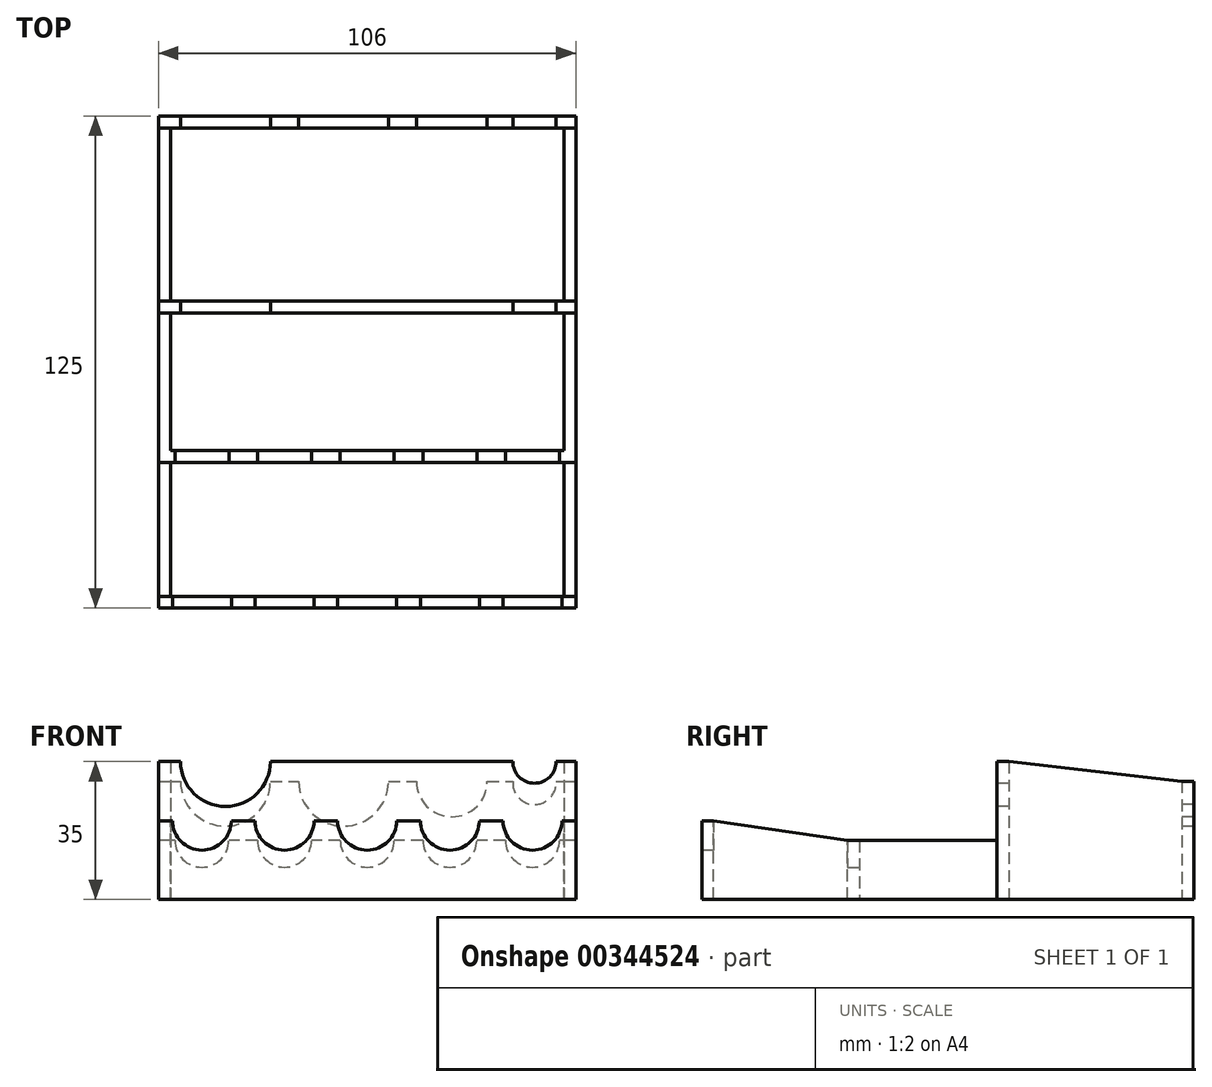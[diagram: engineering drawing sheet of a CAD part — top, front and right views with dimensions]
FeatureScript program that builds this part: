
annotation { "Feature Type Name" : "Feature", "Feature Type Description" : "" }
export const myFeature = defineFeature(function(context is Context, id is Id, definition is map)
    precondition{}
    {
        {
            var Q0;
            Q0=qCreatedBy(makeId("Top.planeOp"),FACE);
            var sketch = newSketch(context, id + "F0", { "sketchPlane" : qUnion([Q0])});
            skLineSegment(sketch, "E0.bottom", {"start": v(53.66, -12.3) * mm, "end": v(-52.34, -12.3) * mm});
            skLineSegment(sketch, "E0.top", {"start": v(53.66, -52.3) * mm, "end": v(-52.34, -52.3) * mm});
            skLineSegment(sketch, "E0.left", {"start": v(53.66, -12.3) * mm, "end": v(53.66, -52.3) * mm});
            skLineSegment(sketch, "E0.right", {"start": v(-52.34, -12.3) * mm, "end": v(-52.34, -52.3) * mm});
            skSolve(sketch);
        }
        {
            var Q0;
            Q0 = qSketchRegion(id + "F0", true);
            extrude(context, id + "F1", {"entities" : qUnion([Q0]), "depth" : 20 * mm});
        }
        {
            var Q0;
            Q0=makeQuery(id+"F1.opExtrude","CAP_FACE",FACE,{"disambiguationData":[OSD([sQuery(id+"F0.wireOp",EDGE,"E0.bottom"),sQuery(id+"F0.wireOp",EDGE,"E0.top"),sQuery(id+"F0.wireOp",EDGE,"E0.left"),sQuery(id+"F0.wireOp",EDGE,"E0.right")])],"isStart":false});
            var sketch = newSketch(context, id + "F2", { "sketchPlane" : qUnion([Q0])});
            skLineSegment(sketch, "E1.0", {"start": v(50.66, -15.3) * mm, "end": v(50.66, -49.3) * mm});
            skLineSegment(sketch, "E1.1", {"start": v(50.66, -15.3) * mm, "end": v(-49.34, -15.3) * mm});
            skLineSegment(sketch, "E1.2", {"start": v(-49.34, -15.3) * mm, "end": v(-49.34, -49.3) * mm});
            skLineSegment(sketch, "E1.3", {"start": v(50.66, -49.3) * mm, "end": v(-49.34, -49.3) * mm});
            skSolve(sketch);
        }
        {
            var Q0;
            Q0=makeQuery(id+"F2.imprint","IMPRINT",FACE,{"disambiguationData":[TD([[makeQuery(id+"F2.imprint","IMPRINT",EDGE,{"derivedFrom":sQuery(id+"F2.wireOp",EDGE,"E1.0")}),-1.0]])]});
            extrude(context, id + "F3", {"entities" : qUnion([Q0]), "operationType" : NewBodyOperationType.REMOVE, "oppositeDirection" : true, "depth" : 20 * mm});
        }
        {
            var Q0;
            Q0=makeQuery(id+"F1.opExtrude","SWEPT_FACE",FACE,{"disambiguationData":[OSD([sQuery(id+"F0.wireOp",EDGE,"E0.top")])]});
            var sketch = newSketch(context, id + "F4", { "sketchPlane" : qUnion([Q0])});
            skCircle(sketch, "E2", {"center": v(-41.34, 20) * mm, "radius": 7.5 * mm});
            skCircle(sketch, "E3.1.0.0", {"center": v(-20.34, 20) * mm, "radius": 7.5 * mm});
            skCircle(sketch, "E3.2.0.0", {"center": v(0.66, 20) * mm, "radius": 7.5 * mm});
            skLineSegment(sketch, "E3.direction1", {"start": v(-41.34, 20) * mm, "end": v(-20.34, 20) * mm, "construction": true});
            skCircle(sketch, "E4.0.3.0", {"center": v(21.66, 20) * mm, "radius": 7.5 * mm});
            skCircle(sketch, "E4.0.4.0", {"center": v(42.66, 20) * mm, "radius": 7.5 * mm});
            skSolve(sketch);
        }
        {
            var Q0;
            {var subQ0=sQuery(id+"F4.wireOp",EDGE,"E2");var subQ1=makeQuery(id+"F1.opExtrude","CAP_EDGE",EDGE,{"disambiguationData":[OSD([sQuery(id+"F0.wireOp",EDGE,"E0.top")])],"isStart":false});var subQ2=makeQuery(id+"F4.imprint","INTERSECT",VERTEX,{"disambiguationData":[OD(0.0)],"derivedFrom":[subQ1,subQ0]});Q0=makeQuery(id+"F4.imprint","IMPRINT",FACE,{"disambiguationData":[TD([[makeQuery(id+"F4.imprint","IMPRINT",EDGE,{"disambiguationData":[TD([[subQ2,-1.0]])],"derivedFrom":subQ0}),1.0]])]});}
            var sketch = newSketch(context, id + "F5", { "sketchPlane" : qUnion([Q0])});
            skSolve(sketch);
        }
        {
            var Q0;
            {var subQ0=sQuery(id+"F4.wireOp",EDGE,"E2");var subQ1=makeQuery(id+"F1.opExtrude","CAP_EDGE",EDGE,{"disambiguationData":[OSD([sQuery(id+"F0.wireOp",EDGE,"E0.top")])],"isStart":false});var subQ2=makeQuery(id+"F4.imprint","INTERSECT",VERTEX,{"disambiguationData":[OD(0.0)],"derivedFrom":[subQ1,subQ0]});Q0=makeQuery(id+"F5.imprint","IMPRINT",FACE,{"disambiguationData":[TD([[makeQuery(id+"F5.imprint","IMPRINT",EDGE,{"derivedFrom":makeQuery(id+"F4.imprint","IMPRINT",EDGE,{"disambiguationData":[TD([[subQ2,-1.0]])],"derivedFrom":subQ0})}),1.0]])]});}
            var Q1;
            {var subQ0=sQuery(id+"F4.wireOp",EDGE,"E4.0.4.0");var subQ1=makeQuery(id+"F1.opExtrude","CAP_EDGE",EDGE,{"disambiguationData":[OSD([sQuery(id+"F0.wireOp",EDGE,"E0.top")])],"isStart":false});var subQ2=makeQuery(id+"F4.imprint","INTERSECT",VERTEX,{"disambiguationData":[OD(0.0)],"derivedFrom":[subQ1,subQ0]});Q1=makeQuery(id+"F4.imprint","IMPRINT",FACE,{"disambiguationData":[TD([[makeQuery(id+"F4.imprint","IMPRINT",EDGE,{"disambiguationData":[TD([[subQ2,1.0]])],"derivedFrom":subQ0}),1.0]])]});}
            var Q2;
            {var subQ0=sQuery(id+"F4.wireOp",EDGE,"E3.1.0.0");var subQ1=makeQuery(id+"F1.opExtrude","CAP_EDGE",EDGE,{"disambiguationData":[OSD([sQuery(id+"F0.wireOp",EDGE,"E0.top")])],"isStart":false});var subQ2=makeQuery(id+"F4.imprint","INTERSECT",VERTEX,{"disambiguationData":[OD(0.0)],"derivedFrom":[subQ1,subQ0]});Q2=makeQuery(id+"F4.imprint","IMPRINT",FACE,{"disambiguationData":[TD([[makeQuery(id+"F4.imprint","IMPRINT",EDGE,{"disambiguationData":[TD([[subQ2,-1.0]])],"derivedFrom":subQ0}),1.0]])]});}
            var Q3;
            {var subQ0=sQuery(id+"F4.wireOp",EDGE,"E3.2.0.0");var subQ1=makeQuery(id+"F1.opExtrude","CAP_EDGE",EDGE,{"disambiguationData":[OSD([sQuery(id+"F0.wireOp",EDGE,"E0.top")])],"isStart":false});var subQ2=makeQuery(id+"F4.imprint","INTERSECT",VERTEX,{"disambiguationData":[OD(0.0)],"derivedFrom":[subQ1,subQ0]});Q3=makeQuery(id+"F4.imprint","IMPRINT",FACE,{"disambiguationData":[TD([[makeQuery(id+"F4.imprint","IMPRINT",EDGE,{"disambiguationData":[TD([[subQ2,-1.0]])],"derivedFrom":subQ0}),1.0]])]});}
            var Q4;
            {var subQ0=sQuery(id+"F4.wireOp",EDGE,"E4.0.3.0");var subQ1=makeQuery(id+"F1.opExtrude","CAP_EDGE",EDGE,{"disambiguationData":[OSD([sQuery(id+"F0.wireOp",EDGE,"E0.top")])],"isStart":false});var subQ2=makeQuery(id+"F4.imprint","INTERSECT",VERTEX,{"disambiguationData":[OD(0.0)],"derivedFrom":[subQ1,subQ0]});Q4=makeQuery(id+"F4.imprint","IMPRINT",FACE,{"disambiguationData":[TD([[makeQuery(id+"F4.imprint","IMPRINT",EDGE,{"disambiguationData":[TD([[subQ2,1.0]])],"derivedFrom":subQ0}),1.0]])]});}
            extrude(context, id + "F6", {"entities" : qUnion([Q0, Q1, Q2, Q3, Q4]), "operationType" : NewBodyOperationType.REMOVE, "oppositeDirection" : true, "depth" : 3 * mm});
        }
        {
            var Q0;
            Q0=makeQuery(id+"F1.opExtrude","SWEPT_FACE",FACE,{"disambiguationData":[OSD([sQuery(id+"F0.wireOp",EDGE,"E0.bottom")])]});
            var sketch = newSketch(context, id + "F7", { "sketchPlane" : qUnion([Q0])});
            skLineSegment(sketch, "E5.bottom", {"start": v(-53.66, 20) * mm, "end": v(52.34, 20) * mm});
            skLineSegment(sketch, "E5.top", {"start": v(-53.66, 15) * mm, "end": v(52.34, 15) * mm});
            skLineSegment(sketch, "E5.left", {"start": v(-53.66, 20) * mm, "end": v(-53.66, 15) * mm});
            skLineSegment(sketch, "E5.right", {"start": v(52.34, 20) * mm, "end": v(52.34, 15) * mm});
            skSolve(sketch);
        }
        {
            var Q0;
            Q0=makeQuery(id+"F7.imprint","IMPRINT",FACE,{"disambiguationData":[TD([[makeQuery(id+"F7.imprint","IMPRINT",EDGE,{"derivedFrom":sQuery(id+"F7.wireOp",EDGE,"E5.bottom")}),-1.0]])]});
            extrude(context, id + "F8", {"entities" : qUnion([Q0]), "operationType" : NewBodyOperationType.REMOVE, "oppositeDirection" : true, "depth" : 3 * mm});
        }
        {
            var Q0;
            {var subQ0=sQuery(id+"F7.wireOp",EDGE,"E5.top");Q0=makeQuery(id+"F7.imprint","IMPRINT",FACE,{"disambiguationData":[TD([[makeQuery(id+"F7.imprint","IMPRINT",EDGE,{"derivedFrom":subQ0}),-1.0]])]});}
            var sketch = newSketch(context, id + "F9", { "sketchPlane" : qUnion([Q0])});
            skCircle(sketch, "E6", {"center": v(41.34, 15) * mm, "radius": 6.85 * mm});
            skCircle(sketch, "E7.1.0.0", {"center": v(20.34, 15) * mm, "radius": 6.85 * mm});
            skCircle(sketch, "E7.2.0.0", {"center": v(-0.66, 15) * mm, "radius": 6.85 * mm});
            skCircle(sketch, "E7.3.0.0", {"center": v(-21.66, 15) * mm, "radius": 6.85 * mm});
            skCircle(sketch, "E7.4.0.0", {"center": v(-42.66, 15) * mm, "radius": 6.85 * mm});
            skLineSegment(sketch, "E7.direction1", {"start": v(41.34, 15) * mm, "end": v(20.34, 15) * mm, "construction": true});
            skSolve(sketch);
        }
        {
            var Q0;
            {var subQ0=sQuery(id+"F9.wireOp",EDGE,"E7.3.0.0");var subQ1=makeQuery(id+"F7.imprint","IMPRINT",EDGE,{"derivedFrom":sQuery(id+"F7.wireOp",EDGE,"E5.top")});var subQ2=makeQuery(id+"F9.imprint","INTERSECT",VERTEX,{"disambiguationData":[OD(0.0)],"derivedFrom":[subQ1,subQ0]});Q0=makeQuery(id+"F9.imprint","IMPRINT",FACE,{"disambiguationData":[TD([[makeQuery(id+"F9.imprint","IMPRINT",EDGE,{"disambiguationData":[TD([[subQ2,-1.0]])],"derivedFrom":subQ0}),1.0]])]});}
            var Q1;
            {var subQ0=sQuery(id+"F9.wireOp",EDGE,"E7.4.0.0");var subQ1=makeQuery(id+"F7.imprint","IMPRINT",EDGE,{"derivedFrom":sQuery(id+"F7.wireOp",EDGE,"E5.top")});var subQ2=makeQuery(id+"F9.imprint","INTERSECT",VERTEX,{"disambiguationData":[OD(0.0)],"derivedFrom":[subQ1,subQ0]});Q1=makeQuery(id+"F9.imprint","IMPRINT",FACE,{"disambiguationData":[TD([[makeQuery(id+"F9.imprint","IMPRINT",EDGE,{"disambiguationData":[TD([[subQ2,-1.0]])],"derivedFrom":subQ0}),1.0]])]});}
            var Q2;
            {var subQ0=sQuery(id+"F9.wireOp",EDGE,"E7.2.0.0");var subQ1=makeQuery(id+"F7.imprint","IMPRINT",EDGE,{"derivedFrom":sQuery(id+"F7.wireOp",EDGE,"E5.top")});var subQ2=makeQuery(id+"F9.imprint","INTERSECT",VERTEX,{"disambiguationData":[OD(0.0)],"derivedFrom":[subQ1,subQ0]});Q2=makeQuery(id+"F9.imprint","IMPRINT",FACE,{"disambiguationData":[TD([[makeQuery(id+"F9.imprint","IMPRINT",EDGE,{"disambiguationData":[TD([[subQ2,1.0]])],"derivedFrom":subQ0}),1.0]])]});}
            var Q3;
            {var subQ0=sQuery(id+"F9.wireOp",EDGE,"E7.1.0.0");var subQ1=makeQuery(id+"F7.imprint","IMPRINT",EDGE,{"derivedFrom":sQuery(id+"F7.wireOp",EDGE,"E5.top")});var subQ2=makeQuery(id+"F9.imprint","INTERSECT",VERTEX,{"disambiguationData":[OD(0.0)],"derivedFrom":[subQ1,subQ0]});Q3=makeQuery(id+"F9.imprint","IMPRINT",FACE,{"disambiguationData":[TD([[makeQuery(id+"F9.imprint","IMPRINT",EDGE,{"disambiguationData":[TD([[subQ2,1.0]])],"derivedFrom":subQ0}),1.0]])]});}
            var Q4;
            {var subQ0=sQuery(id+"F9.wireOp",EDGE,"E6");var subQ1=makeQuery(id+"F7.imprint","IMPRINT",EDGE,{"derivedFrom":sQuery(id+"F7.wireOp",EDGE,"E5.top")});var subQ2=makeQuery(id+"F9.imprint","INTERSECT",VERTEX,{"disambiguationData":[OD(0.0)],"derivedFrom":[subQ1,subQ0]});Q4=makeQuery(id+"F9.imprint","IMPRINT",FACE,{"disambiguationData":[TD([[makeQuery(id+"F9.imprint","IMPRINT",EDGE,{"disambiguationData":[TD([[subQ2,1.0]])],"derivedFrom":subQ0}),1.0]])]});}
            extrude(context, id + "F10", {"entities" : qUnion([Q0, Q1, Q2, Q3, Q4]), "operationType" : NewBodyOperationType.REMOVE, "oppositeDirection" : true, "depth" : 3 * mm});
        }
        {
            var Q0;
            Q0=makeQuery(id+"F1.opExtrude","SWEPT_FACE",FACE,{"disambiguationData":[OSD([sQuery(id+"F0.wireOp",EDGE,"E0.left")])]});
            var sketch = newSketch(context, id + "F11", { "sketchPlane" : qUnion([Q0])});
            skLineSegment(sketch, "E8.bottom", {"start": v(-12.3, 15) * mm, "end": v(22.7, 15) * mm});
            skLineSegment(sketch, "E8.top", {"start": v(-12.3, 0) * mm, "end": v(22.7, 0) * mm});
            skLineSegment(sketch, "E8.left", {"start": v(-12.3, 15) * mm, "end": v(-12.3, 0) * mm});
            skLineSegment(sketch, "E8.right", {"start": v(22.7, 15) * mm, "end": v(22.7, 0) * mm});
            skSolve(sketch);
        }
        {
            var Q0;
            Q0=makeQuery(id+"F1.opExtrude","SWEPT_FACE",FACE,{"disambiguationData":[OSD([sQuery(id+"F0.wireOp",EDGE,"E0.right")])]});
            var sketch = newSketch(context, id + "F12", { "sketchPlane" : qUnion([Q0])});
            skLineSegment(sketch, "E9.bottom", {"start": v(12.3, 15) * mm, "end": v(-22.7, 15) * mm});
            skLineSegment(sketch, "E9.top", {"start": v(12.3, 0) * mm, "end": v(-22.7, 0) * mm});
            skLineSegment(sketch, "E9.left", {"start": v(12.3, 15) * mm, "end": v(12.3, 0) * mm});
            skLineSegment(sketch, "E9.right", {"start": v(-22.7, 15) * mm, "end": v(-22.7, 0) * mm});
            skSolve(sketch);
        }
        {
            var Q0;
            Q0=makeQuery(id+"F12.imprint","IMPRINT",FACE,{"disambiguationData":[TD([[makeQuery(id+"F12.imprint","IMPRINT",EDGE,{"derivedFrom":sQuery(id+"F12.wireOp",EDGE,"E9.bottom")}),1.0]])]});
            extrude(context, id + "F13", {"entities" : qUnion([Q0]), "operationType" : NewBodyOperationType.ADD, "oppositeDirection" : true, "depth" : 3 * mm});
        }
        {
            var Q0;
            Q0=makeQuery(id+"F11.imprint","IMPRINT",FACE,{"disambiguationData":[TD([[makeQuery(id+"F11.imprint","IMPRINT",EDGE,{"derivedFrom":sQuery(id+"F11.wireOp",EDGE,"E8.bottom")}),-1.0]])]});
            extrude(context, id + "F14", {"entities" : qUnion([Q0]), "operationType" : NewBodyOperationType.ADD, "oppositeDirection" : true, "depth" : 3 * mm});
        }
        {
            var Q0;
            Q0=makeQuery(id+"F14.boolean.opBoolean","MERGE",FACE,{"derivedFrom":[makeQuery(id+"F13.boolean.opBoolean","MERGE",FACE,{"derivedFrom":[makeQuery(id+"F1.opExtrude","CAP_FACE",FACE,{"disambiguationData":[OSD([sQuery(id+"F0.wireOp",EDGE,"E0.bottom"),sQuery(id+"F0.wireOp",EDGE,"E0.top"),sQuery(id+"F0.wireOp",EDGE,"E0.left"),sQuery(id+"F0.wireOp",EDGE,"E0.right")])],"isStart":true}),makeQuery(id+"F13.opExtrude","SWEPT_FACE",FACE,{"disambiguationData":[OSD([sQuery(id+"F12.wireOp",EDGE,"E9.top")])]})]}),makeQuery(id+"F14.opExtrude","SWEPT_FACE",FACE,{"disambiguationData":[OSD([sQuery(id+"F11.wireOp",EDGE,"E8.top")])]})]});
            var sketch = newSketch(context, id + "F15", { "sketchPlane" : qUnion([Q0])});
            skLineSegment(sketch, "E10.bottom", {"start": v(-52.34, -22.7) * mm, "end": v(53.66, -22.7) * mm});
            skLineSegment(sketch, "E10.top", {"start": v(-52.34, -72.7) * mm, "end": v(53.66, -72.7) * mm});
            skLineSegment(sketch, "E10.left", {"start": v(-52.34, -22.7) * mm, "end": v(-52.34, -72.7) * mm});
            skLineSegment(sketch, "E10.right", {"start": v(53.66, -22.7) * mm, "end": v(53.66, -72.7) * mm});
            skLineSegment(sketch, "E11.0", {"start": v(-49.34, -25.7) * mm, "end": v(-49.34, -69.7) * mm});
            skLineSegment(sketch, "E11.1", {"start": v(-49.34, -25.7) * mm, "end": v(50.66, -25.7) * mm});
            skLineSegment(sketch, "E11.2", {"start": v(50.66, -25.7) * mm, "end": v(50.66, -69.7) * mm});
            skLineSegment(sketch, "E11.3", {"start": v(-49.34, -69.7) * mm, "end": v(50.66, -69.7) * mm});
            skSolve(sketch);
        }
        {
            var Q0;
            Q0=makeQuery(id+"F15.imprint","IMPRINT",FACE,{"disambiguationData":[TD([[makeQuery(id+"F15.imprint","IMPRINT",EDGE,{"derivedFrom":sQuery(id+"F15.wireOp",EDGE,"E10.top")}),1.0]])]});
            extrude(context, id + "F16", {"entities" : qUnion([Q0]), "oppositeDirection" : true, "depth" : 35 * mm});
        }
        {
            var Q0;
            Q0=makeQuery(id+"F16.opExtrude","SWEPT_FACE",FACE,{"disambiguationData":[OSD([sQuery(id+"F15.wireOp",EDGE,"E10.bottom")])]});
            var sketch = newSketch(context, id + "F17", { "sketchPlane" : qUnion([Q0])});
            skCircle(sketch, "E12", {"center": v(-35.34, 35) * mm, "radius": 11.4 * mm});
            skCircle(sketch, "E13", {"center": v(43.16, 35) * mm, "radius": 5.5 * mm});
            skCircle(sketch, "E14", {"center": v(-7.84, 35) * mm, "radius": 9 * mm});
            skCircle(sketch, "E15.1.0.0", {"center": v(20.69, 35) * mm, "radius": 9 * mm});
            skLineSegment(sketch, "E15.direction1", {"start": v(-7.84, 35) * mm, "end": v(20.69, 35) * mm, "construction": true});
            skSolve(sketch);
        }
        {
            var Q0;
            {var subQ0=sQuery(id+"F17.wireOp",EDGE,"E12");var subQ1=makeQuery(id+"F16.opExtrude","CAP_EDGE",EDGE,{"disambiguationData":[OSD([sQuery(id+"F15.wireOp",EDGE,"E10.bottom")])],"isStart":false});var subQ2=makeQuery(id+"F17.imprint","INTERSECT",VERTEX,{"disambiguationData":[OD(0.0)],"derivedFrom":[subQ1,subQ0]});Q0=makeQuery(id+"F17.imprint","IMPRINT",FACE,{"disambiguationData":[TD([[makeQuery(id+"F17.imprint","IMPRINT",EDGE,{"disambiguationData":[TD([[subQ2,-1.0]])],"derivedFrom":subQ0}),1.0]])]});}
            var Q1;
            {var subQ0=sQuery(id+"F17.wireOp",EDGE,"8cf82a59-2f2f-4f61-8bf0-19492cf728df.1.0.0");var subQ1=makeQuery(id+"F16.opExtrude","CAP_EDGE",EDGE,{"disambiguationData":[OSD([sQuery(id+"F15.wireOp",EDGE,"E10.bottom")])],"isStart":false});var subQ2=makeQuery(id+"F17.imprint","INTERSECT",VERTEX,{"disambiguationData":[OD(0.0)],"derivedFrom":[subQ1,subQ0]});Q1=makeQuery(id+"F17.imprint","IMPRINT",FACE,{"disambiguationData":[TD([[makeQuery(id+"F17.imprint","IMPRINT",EDGE,{"disambiguationData":[TD([[subQ2,-1.0]])],"derivedFrom":subQ0}),1.0]])]});}
            var Q2;
            {var subQ0=sQuery(id+"F17.wireOp",EDGE,"E14");var subQ1=makeQuery(id+"F16.opExtrude","CAP_EDGE",EDGE,{"disambiguationData":[OSD([sQuery(id+"F15.wireOp",EDGE,"E10.bottom")])],"isStart":false});var subQ2=makeQuery(id+"F17.imprint","INTERSECT",VERTEX,{"disambiguationData":[OD(0.0)],"derivedFrom":[subQ1,subQ0]});Q2=makeQuery(id+"F17.imprint","IMPRINT",FACE,{"disambiguationData":[TD([[makeQuery(id+"F17.imprint","IMPRINT",EDGE,{"disambiguationData":[TD([[subQ2,1.0]])],"derivedFrom":subQ0}),1.0]])]});}
            var Q3;
            {var subQ0=sQuery(id+"F17.wireOp",EDGE,"E13");var subQ1=makeQuery(id+"F16.opExtrude","CAP_EDGE",EDGE,{"disambiguationData":[OSD([sQuery(id+"F15.wireOp",EDGE,"E10.bottom")])],"isStart":false});var subQ2=makeQuery(id+"F17.imprint","INTERSECT",VERTEX,{"disambiguationData":[OD(0.0)],"derivedFrom":[subQ1,subQ0]});Q3=makeQuery(id+"F17.imprint","IMPRINT",FACE,{"disambiguationData":[TD([[makeQuery(id+"F17.imprint","IMPRINT",EDGE,{"disambiguationData":[TD([[subQ2,1.0]])],"derivedFrom":subQ0}),1.0]])]});}
            extrude(context, id + "F18", {"entities" : qUnion([Q0, Q1, Q2, Q3]), "operationType" : NewBodyOperationType.REMOVE, "oppositeDirection" : true, "depth" : 3 * mm});
        }
        {
            var Q0;
            Q0=makeQuery(id+"F3.boolean.opBoolean","COPY",FACE,{"derivedFrom":makeQuery(id+"F3.opExtrude","SWEPT_FACE",FACE,{"disambiguationData":[OSD([sQuery(id+"F2.wireOp",EDGE,"E1.0")])]})});
            var sketch = newSketch(context, id + "F19", { "sketchPlane" : qUnion([Q0])});
            skLineSegment(sketch, "E16", {"start": v(49.3, 20) * mm, "end": v(15.3, 15) * mm});
            skSolve(sketch);
        }
        {
            var Q0;
            Q0=makeQuery(id+"F19.imprint","IMPRINT",FACE,{"disambiguationData":[TD([[makeQuery(id+"F19.imprint","IMPRINT",EDGE,{"derivedFrom":sQuery(id+"F19.wireOp",EDGE,"E16")}),-1.0]])]});
            extrude(context, id + "F20", {"entities" : qUnion([Q0]), "operationType" : NewBodyOperationType.REMOVE, "oppositeDirection" : true, "depth" : 3 * mm});
        }
        {
            var Q0;
            Q0=makeQuery(id+"F3.boolean.opBoolean","COPY",FACE,{"derivedFrom":makeQuery(id+"F3.opExtrude","SWEPT_FACE",FACE,{"disambiguationData":[OSD([sQuery(id+"F2.wireOp",EDGE,"E1.2")])]})});
            var sketch = newSketch(context, id + "F21", { "sketchPlane" : qUnion([Q0])});
            skLineSegment(sketch, "E17", {"start": v(-49.3, 20) * mm, "end": v(-15.3, 15) * mm});
            skSolve(sketch);
        }
        {
            var Q0;
            Q0=makeQuery(id+"F21.imprint","IMPRINT",FACE,{"disambiguationData":[TD([[makeQuery(id+"F21.imprint","IMPRINT",EDGE,{"derivedFrom":sQuery(id+"F21.wireOp",EDGE,"E17")}),1.0]])]});
            extrude(context, id + "F22", {"entities" : qUnion([Q0]), "operationType" : NewBodyOperationType.REMOVE, "oppositeDirection" : true, "depth" : 3 * mm});
        }
        {
            var Q0;
            Q0=makeQuery(id+"F16.opExtrude","SWEPT_FACE",FACE,{"disambiguationData":[OSD([sQuery(id+"F15.wireOp",EDGE,"E10.top")])]});
            var sketch = newSketch(context, id + "F23", { "sketchPlane" : qUnion([Q0])});
            skLineSegment(sketch, "E18.bottom", {"start": v(52.34, 35) * mm, "end": v(-53.66, 35) * mm});
            skLineSegment(sketch, "E18.top", {"start": v(52.34, 30) * mm, "end": v(-53.66, 30) * mm});
            skLineSegment(sketch, "E18.left", {"start": v(52.34, 35) * mm, "end": v(52.34, 30) * mm});
            skLineSegment(sketch, "E18.right", {"start": v(-53.66, 35) * mm, "end": v(-53.66, 30) * mm});
            skSolve(sketch);
        }
        {
            var Q0;
            Q0=makeQuery(id+"F23.imprint","IMPRINT",FACE,{"disambiguationData":[TD([[makeQuery(id+"F23.imprint","IMPRINT",EDGE,{"derivedFrom":sQuery(id+"F23.wireOp",EDGE,"E18.bottom")}),1.0]])]});
            extrude(context, id + "F24", {"entities" : qUnion([Q0]), "operationType" : NewBodyOperationType.REMOVE, "oppositeDirection" : true, "depth" : 3 * mm});
        }
        {
            var Q0;
            Q0=makeQuery(id+"F16.opExtrude","SWEPT_FACE",FACE,{"disambiguationData":[OSD([sQuery(id+"F15.wireOp",EDGE,"E11.0")])]});
            var sketch = newSketch(context, id + "F25", { "sketchPlane" : qUnion([Q0])});
            skLineSegment(sketch, "E19", {"start": v(25.7, 35) * mm, "end": v(69.7, 30) * mm});
            skSolve(sketch);
        }
        {
            var Q0;
            Q0=makeQuery(id+"F25.imprint","IMPRINT",FACE,{"disambiguationData":[TD([[makeQuery(id+"F25.imprint","IMPRINT",EDGE,{"derivedFrom":sQuery(id+"F25.wireOp",EDGE,"E19")}),1.0]])]});
            extrude(context, id + "F26", {"entities" : qUnion([Q0]), "operationType" : NewBodyOperationType.REMOVE, "oppositeDirection" : true, "depth" : 3 * mm});
        }
        {
            var Q0;
            Q0=makeQuery(id+"F16.opExtrude","SWEPT_FACE",FACE,{"disambiguationData":[OSD([sQuery(id+"F15.wireOp",EDGE,"E11.2")])]});
            var sketch = newSketch(context, id + "F27", { "sketchPlane" : qUnion([Q0])});
            skLineSegment(sketch, "E20", {"start": v(-25.7, 35) * mm, "end": v(-69.7, 30) * mm});
            skSolve(sketch);
        }
        {
            var Q0;
            Q0=makeQuery(id+"F27.imprint","IMPRINT",FACE,{"disambiguationData":[TD([[makeQuery(id+"F27.imprint","IMPRINT",EDGE,{"derivedFrom":sQuery(id+"F27.wireOp",EDGE,"E20")}),-1.0]])]});
            extrude(context, id + "F28", {"entities" : qUnion([Q0]), "operationType" : NewBodyOperationType.REMOVE, "oppositeDirection" : true, "depth" : 3 * mm});
        }
        {
            var Q0;
            Q0=makeQuery(id+"F16.opExtrude","SWEPT_FACE",FACE,{"disambiguationData":[OSD([sQuery(id+"F15.wireOp",EDGE,"E11.3")])]});
            var sketch = newSketch(context, id + "F29", { "sketchPlane" : qUnion([Q0])});
            skCircle(sketch, "E21", {"center": v(-35.34, 30) * mm, "radius": 11.4 * mm});
            skCircle(sketch, "E22", {"center": v(43.16, 29.6) * mm, "radius": 5.5 * mm});
            skCircle(sketch, "E23.1.0.0", {"center": v(-5.34, 30) * mm, "radius": 11.4 * mm});
            skLineSegment(sketch, "E23.direction1", {"start": v(-35.34, 30) * mm, "end": v(-5.34, 30) * mm, "construction": true});
            skCircle(sketch, "E24", {"center": v(22.16, 30) * mm, "radius": 9 * mm});
            skSolve(sketch);
        }
        {
            var Q0;
            {var subQ0=sQuery(id+"F29.wireOp",EDGE,"E22");var subQ1=sQuery(id+"F23.wireOp",EDGE,"E18.top");var subQ2=makeQuery(id+"F24.boolean.opBoolean","COPY",EDGE,{"disambiguationData":[topologyDisambiguationEdgeConnected([makeQuery(id+"F16.opExtrude","SWEPT_FACE",FACE,{"disambiguationData":[OSD([sQuery(id+"F15.wireOp",EDGE,"E11.3")])]}),makeQuery(id+"F24.opExtrude","SWEPT_FACE",FACE,{"disambiguationData":[OSD([subQ1])]})])],"derivedFrom":makeQuery(id+"F24.opExtrude","CAP_EDGE",EDGE,{"disambiguationData":[OSD([subQ1])],"isStart":false})});var subQ3=makeQuery(id+"F29.imprint","INTERSECT",VERTEX,{"disambiguationData":[OD(0.0)],"derivedFrom":[subQ2,subQ0]});Q0=makeQuery(id+"F29.imprint","IMPRINT",FACE,{"disambiguationData":[TD([[makeQuery(id+"F29.imprint","IMPRINT",EDGE,{"disambiguationData":[TD([[subQ3,1.0]])],"derivedFrom":subQ0}),1.0]])]});}
            var Q1;
            {var subQ0=sQuery(id+"F29.wireOp",EDGE,"E24");var subQ1=sQuery(id+"F23.wireOp",EDGE,"E18.top");var subQ2=makeQuery(id+"F24.boolean.opBoolean","COPY",EDGE,{"disambiguationData":[topologyDisambiguationEdgeConnected([makeQuery(id+"F16.opExtrude","SWEPT_FACE",FACE,{"disambiguationData":[OSD([sQuery(id+"F15.wireOp",EDGE,"E11.3")])]}),makeQuery(id+"F24.opExtrude","SWEPT_FACE",FACE,{"disambiguationData":[OSD([subQ1])]})])],"derivedFrom":makeQuery(id+"F24.opExtrude","CAP_EDGE",EDGE,{"disambiguationData":[OSD([subQ1])],"isStart":false})});var subQ3=makeQuery(id+"F29.imprint","INTERSECT",VERTEX,{"disambiguationData":[OD(0.0)],"derivedFrom":[subQ2,subQ0]});Q1=makeQuery(id+"F29.imprint","IMPRINT",FACE,{"disambiguationData":[TD([[makeQuery(id+"F29.imprint","IMPRINT",EDGE,{"disambiguationData":[TD([[subQ3,1.0]])],"derivedFrom":subQ0}),1.0]])]});}
            var Q2;
            {var subQ0=sQuery(id+"F29.wireOp",EDGE,"E23.1.0.0");var subQ1=sQuery(id+"F23.wireOp",EDGE,"E18.top");var subQ2=makeQuery(id+"F24.boolean.opBoolean","COPY",EDGE,{"disambiguationData":[topologyDisambiguationEdgeConnected([makeQuery(id+"F16.opExtrude","SWEPT_FACE",FACE,{"disambiguationData":[OSD([sQuery(id+"F15.wireOp",EDGE,"E11.3")])]}),makeQuery(id+"F24.opExtrude","SWEPT_FACE",FACE,{"disambiguationData":[OSD([subQ1])]})])],"derivedFrom":makeQuery(id+"F24.opExtrude","CAP_EDGE",EDGE,{"disambiguationData":[OSD([subQ1])],"isStart":false})});var subQ3=makeQuery(id+"F29.imprint","INTERSECT",VERTEX,{"disambiguationData":[OD(0.0)],"derivedFrom":[subQ2,subQ0]});Q2=makeQuery(id+"F29.imprint","IMPRINT",FACE,{"disambiguationData":[TD([[makeQuery(id+"F29.imprint","IMPRINT",EDGE,{"disambiguationData":[TD([[subQ3,-1.0]])],"derivedFrom":subQ0}),1.0]])]});}
            var Q3;
            {var subQ0=sQuery(id+"F29.wireOp",EDGE,"E21");var subQ1=sQuery(id+"F23.wireOp",EDGE,"E18.top");var subQ2=makeQuery(id+"F24.boolean.opBoolean","COPY",EDGE,{"disambiguationData":[topologyDisambiguationEdgeConnected([makeQuery(id+"F16.opExtrude","SWEPT_FACE",FACE,{"disambiguationData":[OSD([sQuery(id+"F15.wireOp",EDGE,"E11.3")])]}),makeQuery(id+"F24.opExtrude","SWEPT_FACE",FACE,{"disambiguationData":[OSD([subQ1])]})])],"derivedFrom":makeQuery(id+"F24.opExtrude","CAP_EDGE",EDGE,{"disambiguationData":[OSD([subQ1])],"isStart":false})});var subQ3=makeQuery(id+"F29.imprint","INTERSECT",VERTEX,{"disambiguationData":[OD(0.0)],"derivedFrom":[subQ2,subQ0]});Q3=makeQuery(id+"F29.imprint","IMPRINT",FACE,{"disambiguationData":[TD([[makeQuery(id+"F29.imprint","IMPRINT",EDGE,{"disambiguationData":[TD([[subQ3,-1.0]])],"derivedFrom":subQ0}),1.0]])]});}
            extrude(context, id + "F30", {"entities" : qUnion([Q0, Q1, Q2, Q3]), "operationType" : NewBodyOperationType.REMOVE, "oppositeDirection" : true, "depth" : 3 * mm});
        }
    });
